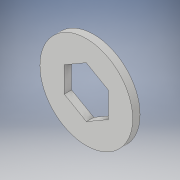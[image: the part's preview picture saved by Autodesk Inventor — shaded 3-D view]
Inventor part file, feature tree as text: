
AUTODESK INVENTOR PART (.ipt)
format: ipt  version: 2018 (Build 220112000, 112)  size: 103,424 bytes
history: native  units: in
note: dims shown in document units (in); Inventor stores cm internally (conversion verified against a paired STEP export)
features: extrude x1, sketch x1
ambient origin geometry x8: Origin, YZ Plane, XZ Plane, XY Plane, X Axis, Y Axis, Z Axis, Center Point
bodies: Body1 (feature_tree)
feature tree (2):
  extrude  "Extrusion2"  Depth=0.0625in
  sketch  "Sketch1"  dims[d1=0.787in d4=0.1875in d5=0.0625in d6=0.0in]
